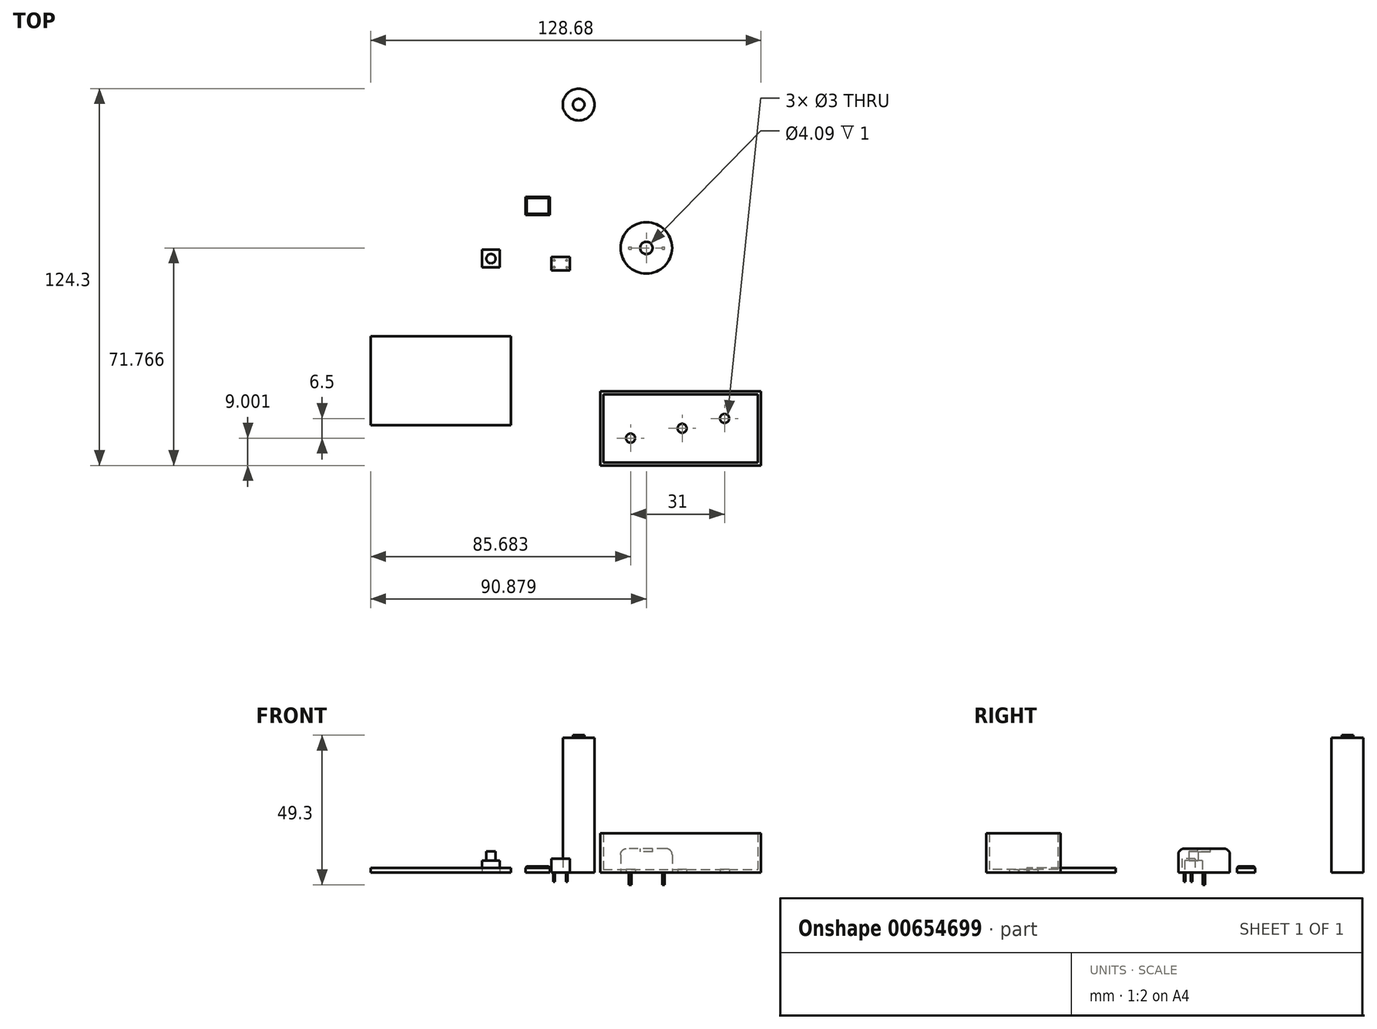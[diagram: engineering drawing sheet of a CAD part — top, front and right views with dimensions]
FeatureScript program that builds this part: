
annotation { "Feature Type Name" : "Feature", "Feature Type Description" : "" }
export const myFeature = defineFeature(function(context is Context, id is Id, definition is map)
    precondition{}
    {
        {
            var Q0;
            Q0=qCreatedBy(makeId("Top.planeOp"),FACE);
            var sketch = newSketch(context, id + "F0", { "sketchPlane" : qUnion([Q0])});
            skLineSegment(sketch, "E0.bottom", {"start": v(3.05, 2.2) * mm, "end": v(-3.05, 2.2) * mm});
            skLineSegment(sketch, "E0.top", {"start": v(3.05, -2.2) * mm, "end": v(-3.05, -2.2) * mm});
            skLineSegment(sketch, "E0.left", {"start": v(3.05, 2.2) * mm, "end": v(3.05, -2.2) * mm});
            skLineSegment(sketch, "E0.right", {"start": v(-3.05, 2.2) * mm, "end": v(-3.05, -2.2) * mm});
            skPoint(sketch, "E0.middle", {"position": v(0, 0) * mm});
            skSolve(sketch);
        }
        {
            var Q0;
            Q0=qSketchRegion(id+"F0",true);
            extrude(context, id + "F1", {"entities" : qUnion([Q0]), "depth" : 4.65 * mm, "offsetDistance" : 25 * mm});
        }
        {
            var Q0;
            Q0=makeQuery(id+"F1.opExtrude","CAP_FACE",FACE,{"disambiguationData":[OSD([sQuery(id+"F0.wireOp",EDGE,"E0.bottom"),sQuery(id+"F0.wireOp",EDGE,"E0.top"),sQuery(id+"F0.wireOp",EDGE,"E0.left"),sQuery(id+"F0.wireOp",EDGE,"E0.right")])],"isStart":true});
            var sketch = newSketch(context, id + "F2", { "sketchPlane" : qUnion([Q0])});
            skLineSegment(sketch, "E1.bottom", {"start": v(-1.92, 0.98) * mm, "end": v(-2.36, 0.98) * mm});
            skLineSegment(sketch, "E1.top", {"start": v(-1.92, 1.47) * mm, "end": v(-2.36, 1.47) * mm});
            skLineSegment(sketch, "E1.left", {"start": v(-1.92, 0.98) * mm, "end": v(-1.92, 1.47) * mm});
            skLineSegment(sketch, "E1.right", {"start": v(-2.36, 0.98) * mm, "end": v(-2.36, 1.47) * mm});
            skPoint(sketch, "E1.middle", {"position": v(-2.14, 1.23) * mm});
            skLineSegment(sketch, "E2.bottom", {"start": v(-1.92, -1.28) * mm, "end": v(-2.36, -1.28) * mm});
            skLineSegment(sketch, "E2.top", {"start": v(-1.92, -0.83) * mm, "end": v(-2.36, -0.83) * mm});
            skLineSegment(sketch, "E2.left", {"start": v(-1.92, -1.28) * mm, "end": v(-1.92, -0.83) * mm});
            skLineSegment(sketch, "E2.right", {"start": v(-2.36, -1.28) * mm, "end": v(-2.36, -0.83) * mm});
            skPoint(sketch, "E2.middle", {"position": v(-2.14, -1.05) * mm});
            skPoint(sketch, "E2.middle.positionSnap0", {"position": v(-2.14, 0.98) * mm});
            skPoint(sketch, "E2.centerSnap0", {"position": v(-2.14, 0.98) * mm});
            skLineSegment(sketch, "E3.bottom", {"start": v(1.82, 0.98) * mm, "end": v(2.27, 0.98) * mm});
            skLineSegment(sketch, "E3.top", {"start": v(1.82, 1.47) * mm, "end": v(2.27, 1.47) * mm});
            skLineSegment(sketch, "E3.left", {"start": v(1.82, 0.98) * mm, "end": v(1.82, 1.47) * mm});
            skLineSegment(sketch, "E3.right", {"start": v(2.27, 0.98) * mm, "end": v(2.27, 1.47) * mm});
            skPoint(sketch, "E3.middle", {"position": v(2.05, 1.23) * mm});
            skPoint(sketch, "E3.middle.positionSnap0", {"position": v(-1.92, 1.23) * mm});
            skPoint(sketch, "E3.centerSnap0", {"position": v(-1.92, 1.23) * mm});
            skLineSegment(sketch, "E4.bottom", {"start": v(2.27, -0.83) * mm, "end": v(1.82, -0.83) * mm});
            skLineSegment(sketch, "E4.top", {"start": v(2.27, -1.28) * mm, "end": v(1.82, -1.28) * mm});
            skLineSegment(sketch, "E4.left", {"start": v(2.27, -0.83) * mm, "end": v(2.27, -1.28) * mm});
            skLineSegment(sketch, "E4.right", {"start": v(1.82, -0.83) * mm, "end": v(1.82, -1.28) * mm});
            skPoint(sketch, "E4.middle", {"position": v(2.05, -1.05) * mm});
            skPoint(sketch, "E4.middle.positionSnap0", {"position": v(-1.92, -1.05) * mm});
            skPoint(sketch, "E4.centerSnap0", {"position": v(-1.92, -1.05) * mm});
            skSolve(sketch);
        }
        {
            var Q0;
            Q0=qSketchRegion(id+"F2",true);
            extrude(context, id + "F3", {"entities" : qUnion([Q0]), "operationType" : NewBodyOperationType.ADD, "depth" : 3 * mm, "offsetDistance" : 25 * mm});
        }
        {
            var Q0;
            Q0=qCreatedBy(makeId("Top.planeOp"),FACE);
            var sketch = newSketch(context, id + "F4", { "sketchPlane" : qUnion([Q0])});
            skLineSegment(sketch, "E5.bottom", {"start": v(-25.9, 4.55) * mm, "end": v(-20.05, 4.55) * mm});
            skLineSegment(sketch, "E5.top", {"start": v(-25.9, -1.3) * mm, "end": v(-20.05, -1.3) * mm});
            skLineSegment(sketch, "E5.left", {"start": v(-25.9, 4.55) * mm, "end": v(-25.9, -1.3) * mm});
            skLineSegment(sketch, "E5.right", {"start": v(-20.05, 4.55) * mm, "end": v(-20.05, -1.3) * mm});
            skSolve(sketch);
        }
        {
            var Q0;
            Q0=makeQuery(id+"F4.imprint","IMPRINT",FACE,{"disambiguationData":[TD([[makeQuery(id+"F4.imprint","IMPRINT",EDGE,{"derivedFrom":sQuery(id+"F4.wireOp",EDGE,"E5.bottom")}),-1.0]])]});
            extrude(context, id + "F5", {"entities" : qUnion([Q0]), "depth" : 4 * mm, "offsetDistance" : 25 * mm});
        }
        {
            var Q0;
            Q0=makeQuery(id+"F5.opExtrude","CAP_FACE",FACE,{"disambiguationData":[OSD([sQuery(id+"F4.wireOp",EDGE,"E5.bottom"),sQuery(id+"F4.wireOp",EDGE,"E5.top"),sQuery(id+"F4.wireOp",EDGE,"E5.left"),sQuery(id+"F4.wireOp",EDGE,"E5.right")])],"isStart":false});
            var sketch = newSketch(context, id + "F6", { "sketchPlane" : qUnion([Q0])});
            skCircle(sketch, "E6", {"center": v(-22.97, 1.62) * mm, "radius": 1.53 * mm});
            skPoint(sketch, "E6.centerSnap0", {"position": v(-25.9, 1.62) * mm});
            skPoint(sketch, "E6.centerSnap1", {"position": v(-22.97, 4.55) * mm});
            skSolve(sketch);
        }
        {
            var Q0;
            Q0=makeQuery(id+"F6.imprint","IMPRINT",FACE,{"disambiguationData":[TD([[makeQuery(id+"F6.imprint","IMPRINT",EDGE,{"derivedFrom":sQuery(id+"F6.wireOp",EDGE,"E6")}),1.0]])]});
            extrude(context, id + "F7", {"entities" : qUnion([Q0]), "operationType" : NewBodyOperationType.ADD, "depth" : 3 * mm, "offsetDistance" : 25 * mm});
        }
        {
            var Q0;
            Q0=qCreatedBy(makeId("Top.planeOp"),FACE);
            var sketch = newSketch(context, id + "F8", { "sketchPlane" : qUnion([Q0])});
            skCircle(sketch, "E7", {"center": v(28.26, 5.17) * mm, "radius": 8.5 * mm});
            skSolve(sketch);
        }
        {
            var Q0;
            Q0 = qSketchRegion(id + "F8", true);
            extrude(context, id + "F9", {"entities" : qUnion([Q0]), "depth" : 7.9 * mm, "offsetDistance" : 25 * mm});
        }
        {
            var Q0;
            Q0=makeQuery(id+"F9.opExtrude","CAP_EDGE",EDGE,{"disambiguationData":[OSD([sQuery(id+"F8.wireOp",EDGE,"E7")])],"isStart":false});
            fillet(context, id + "F10", {"entities" : qUnion([Q0]), "radius" : 2 * mm, "tangentPropagation" : true, "allowEdgeOverflow" : false});
        }
        {
            var Q0;
            Q0=makeQuery(id+"F9.opExtrude","CAP_FACE",FACE,{"disambiguationData":[OSD([sQuery(id+"F8.wireOp",EDGE,"E7")])],"isStart":false});
            var sketch = newSketch(context, id + "F11", { "sketchPlane" : qUnion([Q0])});
            skCircle(sketch, "E8", {"center": v(28.26, 5.17) * mm, "radius": 2.05 * mm});
            skSolve(sketch);
        }
        {
            var Q0;
            Q0=makeQuery(id+"F11.imprint","IMPRINT",FACE,{"disambiguationData":[TD([[makeQuery(id+"F11.imprint","IMPRINT",EDGE,{"derivedFrom":sQuery(id+"F11.wireOp",EDGE,"E8")}),1.0]])]});
            extrude(context, id + "F12", {"entities" : qUnion([Q0]), "operationType" : NewBodyOperationType.REMOVE, "oppositeDirection" : true, "depth" : 1 * mm, "offsetDistance" : 25 * mm});
        }
        {
            var Q0;
            Q0=makeQuery(id+"F9.opExtrude","CAP_FACE",FACE,{"disambiguationData":[OSD([sQuery(id+"F8.wireOp",EDGE,"E7")])],"isStart":true});
            var sketch = newSketch(context, id + "F13", { "sketchPlane" : qUnion([Q0])});
            skLineSegment(sketch, "E9.bottom", {"start": v(22.53, -4.7) * mm, "end": v(23.3, -4.7) * mm});
            skLineSegment(sketch, "E9.top", {"start": v(22.53, -5.51) * mm, "end": v(23.3, -5.51) * mm});
            skLineSegment(sketch, "E9.left", {"start": v(22.53, -4.7) * mm, "end": v(22.53, -5.51) * mm});
            skLineSegment(sketch, "E9.right", {"start": v(23.3, -4.7) * mm, "end": v(23.3, -5.51) * mm});
            skLineSegment(sketch, "E10.bottom", {"start": v(33.46, -4.75) * mm, "end": v(34.23, -4.75) * mm});
            skLineSegment(sketch, "E10.top", {"start": v(33.46, -5.45) * mm, "end": v(34.23, -5.45) * mm});
            skLineSegment(sketch, "E10.left", {"start": v(33.46, -4.75) * mm, "end": v(33.46, -5.45) * mm});
            skLineSegment(sketch, "E10.right", {"start": v(34.23, -4.75) * mm, "end": v(34.23, -5.45) * mm});
            skSolve(sketch);
        }
        {
            var Q0;
            Q0 = qSketchRegion(id + "F13", true);
            extrude(context, id + "F14", {"entities" : qUnion([Q0]), "operationType" : NewBodyOperationType.ADD, "depth" : 4 * mm, "offsetDistance" : 25 * mm});
        }
        {
            var Q0;
            Q0=qCreatedBy(makeId("Top.planeOp"),FACE);
            var sketch = newSketch(context, id + "F15", { "sketchPlane" : qUnion([Q0])});
            skLineSegment(sketch, "E11.bottom", {"start": v(-11.57, 22.04) * mm, "end": v(-3.57, 22.04) * mm});
            skLineSegment(sketch, "E11.top", {"start": v(-11.57, 16.04) * mm, "end": v(-3.57, 16.04) * mm});
            skLineSegment(sketch, "E11.left", {"start": v(-11.57, 22.04) * mm, "end": v(-11.57, 16.04) * mm});
            skLineSegment(sketch, "E11.right", {"start": v(-3.57, 22.04) * mm, "end": v(-3.57, 16.04) * mm});
            skSolve(sketch);
        }
        {
            var Q0;
            Q0 = qSketchRegion(id + "F15", true);
            extrude(context, id + "F16", {"entities" : qUnion([Q0]), "depth" : 2 * mm, "offsetDistance" : 25 * mm});
        }
        {
            var Q0;
            Q0=makeQuery(id+"F16.opExtrude","CAP_EDGE",EDGE,{"disambiguationData":[OSD([sQuery(id+"F15.wireOp",EDGE,"E11.top")])],"isStart":false});
            var Q1;
            Q1=makeQuery(id+"F16.opExtrude","CAP_EDGE",EDGE,{"disambiguationData":[OSD([sQuery(id+"F15.wireOp",EDGE,"E11.bottom")])],"isStart":false});
            var Q2;
            Q2=makeQuery(id+"F16.opExtrude","CAP_EDGE",EDGE,{"disambiguationData":[OSD([sQuery(id+"F15.wireOp",EDGE,"E11.right")])],"isStart":false});
            var Q3;
            Q3=makeQuery(id+"F16.opExtrude","CAP_EDGE",EDGE,{"disambiguationData":[OSD([sQuery(id+"F15.wireOp",EDGE,"E11.left")])],"isStart":false});
            chamfer(context, id + "F17", {"entities" : qUnion([Q0, Q1, Q2, Q3]), "width" : 0.4 * mm, "tangentPropagation" : true});
        }
        {
            var Q0;
            Q0=qCreatedBy(makeId("Top.planeOp"),FACE);
            var sketch = newSketch(context, id + "F18", { "sketchPlane" : qUnion([Q0])});
            skCircle(sketch, "E12", {"center": v(5.95, 52.45) * mm, "radius": 5.25 * mm});
            skSolve(sketch);
        }
        {
            var Q0;
            Q0=makeQuery(id+"F18.imprint","IMPRINT",FACE,{"disambiguationData":[TD([[makeQuery(id+"F18.imprint","IMPRINT",EDGE,{"derivedFrom":sQuery(id+"F18.wireOp",EDGE,"E12")}),1.0]])]});
            extrude(context, id + "F19", {"entities" : qUnion([Q0]), "depth" : 44.5 * mm, "offsetDistance" : 25 * mm});
        }
        {
            var Q0;
            Q0=makeQuery(id+"F19.opExtrude","CAP_FACE",FACE,{"disambiguationData":[OSD([sQuery(id+"F18.wireOp",EDGE,"E12")])],"isStart":false});
            var sketch = newSketch(context, id + "F20", { "sketchPlane" : qUnion([Q0])});
            skCircle(sketch, "E13", {"center": v(5.95, 52.45) * mm, "radius": 1.9 * mm});
            skSolve(sketch);
        }
        {
            var Q0;
            Q0=makeQuery(id+"F20.imprint","IMPRINT",FACE,{"disambiguationData":[TD([[makeQuery(id+"F20.imprint","IMPRINT",EDGE,{"derivedFrom":sQuery(id+"F20.wireOp",EDGE,"E13")}),1.0]])]});
            extrude(context, id + "F21", {"entities" : qUnion([Q0]), "operationType" : NewBodyOperationType.ADD, "depth" : 0.8 * mm, "offsetDistance" : 25 * mm});
        }
        {
            var Q0;
            Q0=qCreatedBy(makeId("Top.planeOp"),FACE);
            var sketch = newSketch(context, id + "F22", { "sketchPlane" : qUnion([Q0])});
            skLineSegment(sketch, "E14.bottom", {"start": v(-62.62, -23.97) * mm, "end": v(-16.42, -23.97) * mm});
            skLineSegment(sketch, "E14.top", {"start": v(-62.62, -53.32) * mm, "end": v(-16.42, -53.32) * mm});
            skLineSegment(sketch, "E14.left", {"start": v(-62.62, -23.97) * mm, "end": v(-62.62, -53.32) * mm});
            skLineSegment(sketch, "E14.right", {"start": v(-16.42, -23.97) * mm, "end": v(-16.42, -53.32) * mm});
            skSolve(sketch);
        }
        {
            var Q0;
            Q0 = qSketchRegion(id + "F22", true);
            extrude(context, id + "F23", {"entities" : qUnion([Q0]), "depth" : 1.5 * mm, "offsetDistance" : 25 * mm});
        }
        {
            var Q0;
            Q0=qCreatedBy(makeId("Top.planeOp"),FACE);
            var sketch = newSketch(context, id + "F24", { "sketchPlane" : qUnion([Q0])});
            skLineSegment(sketch, "E15.bottom", {"start": v(13.06, -42.1) * mm, "end": v(66.06, -42.1) * mm});
            skLineSegment(sketch, "E15.top", {"start": v(13.06, -66.6) * mm, "end": v(66.06, -66.6) * mm});
            skLineSegment(sketch, "E15.left", {"start": v(13.06, -42.1) * mm, "end": v(13.06, -66.6) * mm});
            skLineSegment(sketch, "E15.right", {"start": v(66.06, -42.1) * mm, "end": v(66.06, -66.6) * mm});
            skSolve(sketch);
        }
        {
            var Q0;
            Q0=makeQuery(id+"F24.imprint","IMPRINT",FACE,{"disambiguationData":[TD([[makeQuery(id+"F24.imprint","IMPRINT",EDGE,{"derivedFrom":sQuery(id+"F24.wireOp",EDGE,"E15.bottom")}),-1.0]])]});
            extrude(context, id + "F25", {"entities" : qUnion([Q0]), "depth" : 1 * mm, "offsetDistance" : 25 * mm});
        }
        {
            var Q0;
            Q0=makeQuery(id+"F25.opExtrude","CAP_FACE",FACE,{"disambiguationData":[OSD([sQuery(id+"F24.wireOp",EDGE,"E15.bottom"),sQuery(id+"F24.wireOp",EDGE,"E15.top"),sQuery(id+"F24.wireOp",EDGE,"E15.left"),sQuery(id+"F24.wireOp",EDGE,"E15.right")])],"isStart":false});
            var sketch = newSketch(context, id + "F26", { "sketchPlane" : qUnion([Q0])});
            skLineSegment(sketch, "E16.bottom", {"start": v(14.06, -43.1) * mm, "end": v(65.06, -43.1) * mm});
            skLineSegment(sketch, "E16.top", {"start": v(14.06, -65.6) * mm, "end": v(65.06, -65.6) * mm});
            skLineSegment(sketch, "E16.left", {"start": v(14.06, -43.1) * mm, "end": v(14.06, -65.6) * mm});
            skLineSegment(sketch, "E16.right", {"start": v(65.06, -43.1) * mm, "end": v(65.06, -65.6) * mm});
            skSolve(sketch);
        }
        {
            var Q0;
            Q0=makeQuery(id+"F26.imprint","IMPRINT",FACE,{"disambiguationData":[TD([[makeQuery(id+"F26.imprint","IMPRINT",EDGE,{"derivedFrom":sQuery(id+"F26.wireOp",EDGE,"E16.bottom")}),1.0]])]});
            extrude(context, id + "F27", {"entities" : qUnion([Q0]), "operationType" : NewBodyOperationType.ADD, "depth" : 12 * mm, "offsetDistance" : 25 * mm});
        }
        {
            var Q0;
            Q0=makeQuery(id+"F25.opExtrude","CAP_FACE",FACE,{"disambiguationData":[OSD([sQuery(id+"F24.wireOp",EDGE,"E15.bottom"),sQuery(id+"F24.wireOp",EDGE,"E15.top"),sQuery(id+"F24.wireOp",EDGE,"E15.left"),sQuery(id+"F24.wireOp",EDGE,"E15.right")])],"isStart":true});
            var sketch = newSketch(context, id + "F28", { "sketchPlane" : qUnion([Q0])});
            skCircle(sketch, "E17", {"center": v(23.06, 57.6) * mm, "radius": 1.5 * mm});
            skCircle(sketch, "E18", {"center": v(54.06, 51.1) * mm, "radius": 1.5 * mm});
            skCircle(sketch, "E19", {"center": v(40.06, 54.35) * mm, "radius": 1.5 * mm});
            skSolve(sketch);
        }
        {
            var Q0;
            Q0=makeQuery(id+"F28.imprint","IMPRINT",FACE,{"disambiguationData":[TD([[makeQuery(id+"F28.imprint","IMPRINT",EDGE,{"derivedFrom":sQuery(id+"F28.wireOp",EDGE,"E17")}),1.0]])]});
            var Q1;
            Q1=makeQuery(id+"F28.imprint","IMPRINT",FACE,{"disambiguationData":[TD([[makeQuery(id+"F28.imprint","IMPRINT",EDGE,{"derivedFrom":sQuery(id+"F28.wireOp",EDGE,"E19")}),1.0]])]});
            var Q2;
            Q2=makeQuery(id+"F28.imprint","IMPRINT",FACE,{"disambiguationData":[TD([[makeQuery(id+"F28.imprint","IMPRINT",EDGE,{"derivedFrom":sQuery(id+"F28.wireOp",EDGE,"E18")}),1.0]])]});
            extrude(context, id + "F29", {"entities" : qUnion([Q0, Q1, Q2]), "operationType" : NewBodyOperationType.REMOVE, "endBound" : BoundingType.UP_TO_NEXT, "oppositeDirection" : true, "depth" : 25 * mm, "offsetDistance" : 25 * mm});
        }
    });
